# Revit family: LEGRAND_NON INTERLOCKED SOCKETS_SURFACE MOUNTED_IP66_400
name_source: partatom
category: Installations électriques
revit_build: Autodesk Revit 2018 (Build: 20170223_1515(x64)
units: mm (PartAtom-declared; Revit-internal decimal feet)

## family parameters
Conserver l'orientation des annotations = Non
Cote de connecteur circulaire = Utiliser le diamètre
Couper avec des vides une fois chargée = Non
Hôte = Face
Partagée = Non
Point de calcul de pièce = Non
Type d'élément = Normal

## types (10) — shared parameters
Description = international standard socket for flush or surface mounting with accessory allows the connection of power devices
Dia bouchon = 90 mm  [stored 0.295276 ft]
Elévation par défaut = 1000 mm  [stored 3.28084 ft]
Fabricant = Legrand
Flush E or Surface mounting S = flush and surface mounting
General Conditions of Use = https://export.legrand.com
L2 = 40 mm  [stored 0.131234 ft]
Maximum installation temperature = 40°C
Maximum use temperature = 100°C
Minimum installation temperature = -20°C
Minimum use temperature = -50°C
RAY BOUCHON = 45 mm  [stored 0.147638 ft]
Ray = 28 mm
Standard IEC or NFC = IEC
Tension V = 400 V  50/60 Hz red
characteristic color = red
connecting type = screw terminals
dIA = 56 mm
halogen free = Non
material of box = plastic
protection class IP = IP66/67-55
resistance to chocks IK = 09

## per-type parameters (varying)
| type | Modèle | Number of poles | Position of earth h | depth for flush mounting mm | depth mm | h1 | height mm | horizontal fixing distance mm | intensity A | vertical fixing distance mm | width mm |
| panel mounting socket Hypra   IP66/67-55   16 A   380/415 V   3P+E   plast surface box for passage wiring | 051130 | 4 | 6 | 75 mm | 145 mm | 109 mm | 182 mm | 60 mm | 16 A | 70 mm | 86 mm |
| panel mounting socket Hypra   IP66/67-55   16 A   380/415 V   3P+N+E   plast surface box for passage wiring | 051131 | 6 | 6 | 75 mm | 145 mm | 109 mm | 182 mm | 60 mm | 16 A | 70 mm | 86 mm |
| panel mounting socket single fixing center Hypra  IP66/67-55  32 A   380/415 V   3P+E   plast surface box for passage wiring | 053050 | 4 | 6 | 90 mm  [stored 0.295276 ft] | 160 mm  [stored 0.524934 ft] | 97 mm | 162 mm | 70 mm | 32 A | 70 mm | 102 mm |
| panel mounting socket single fixing center Hypra  IP66/67-55  32 A  380/415 V   3P +N+E  plast surface box for passage wiring | 053051 | 5 | 6 | 90 mm  [stored 0.295276 ft] | 160 mm  [stored 0.524934 ft] | 97 mm | 162 mm | 70 mm | 32 A | 70 mm | 102 mm |
| panel mounting socket Hypra  IP 66/67-55   63A   380/415 V   3P+E   plast surface box for passage wiring | 059427 | 4 | 9 | 150 mm | 225 mm | 180 mm  [stored 0.590551 ft] | 300 mm | 77 mm | 63 A | 85 mm | 170 mm |
| panel mounting socket Hypra  IP 66/67-55   63A   380/415 V   3P+N+E   plast surface box for passage wiring | 059428 | 4 | 9 | 150 mm | 225 mm | 180 mm  [stored 0.590551 ft] | 300 mm | 77 mm | 63 A | 85 mm | 170 mm |
| panel mounting socket Hypra   IP66/67-55   16 A   380/415 V   3P+E   plast surface mounting | 051130 | 4 | 6 | 58 mm | 115 mm | 64 mm | 106 mm | 60 mm | 16 A | 70 mm | 74 mm |
| panel mounting socket Hypra   IP66/67-55   16 A   380/415 V   3P+N+E   plast surface mounting | 051131 | 6 | 6 | 58 mm | 115 mm | 64 mm | 106 mm | 60 mm | 16 A | 70 mm | 74 mm |
| panel mounting socket single fixing center Hypra  IP66/67-55  32 A   380/415 V   3P+E  plast surface mounting | 053050 | 4 | 6 | 90 mm  [stored 0.295276 ft] | 160 mm  [stored 0.524934 ft] | 97 mm | 162 mm | 70 mm | 32 A | 70 mm | 102 mm |
| panel mounting socket single fixing center Hypra  IP66/67-55  32 A  380/415 V   3P+N+E  plast surface mounting | 053051 | 5 | 6 | 90 mm  [stored 0.295276 ft] | 160 mm  [stored 0.524934 ft] | 97 mm | 162 mm | 70 mm | 32 A | 70 mm | 102 mm |

note: [stored X ft] marks values corroborated as IEEE doubles in the binary element streams (Revit-internal decimal feet)
